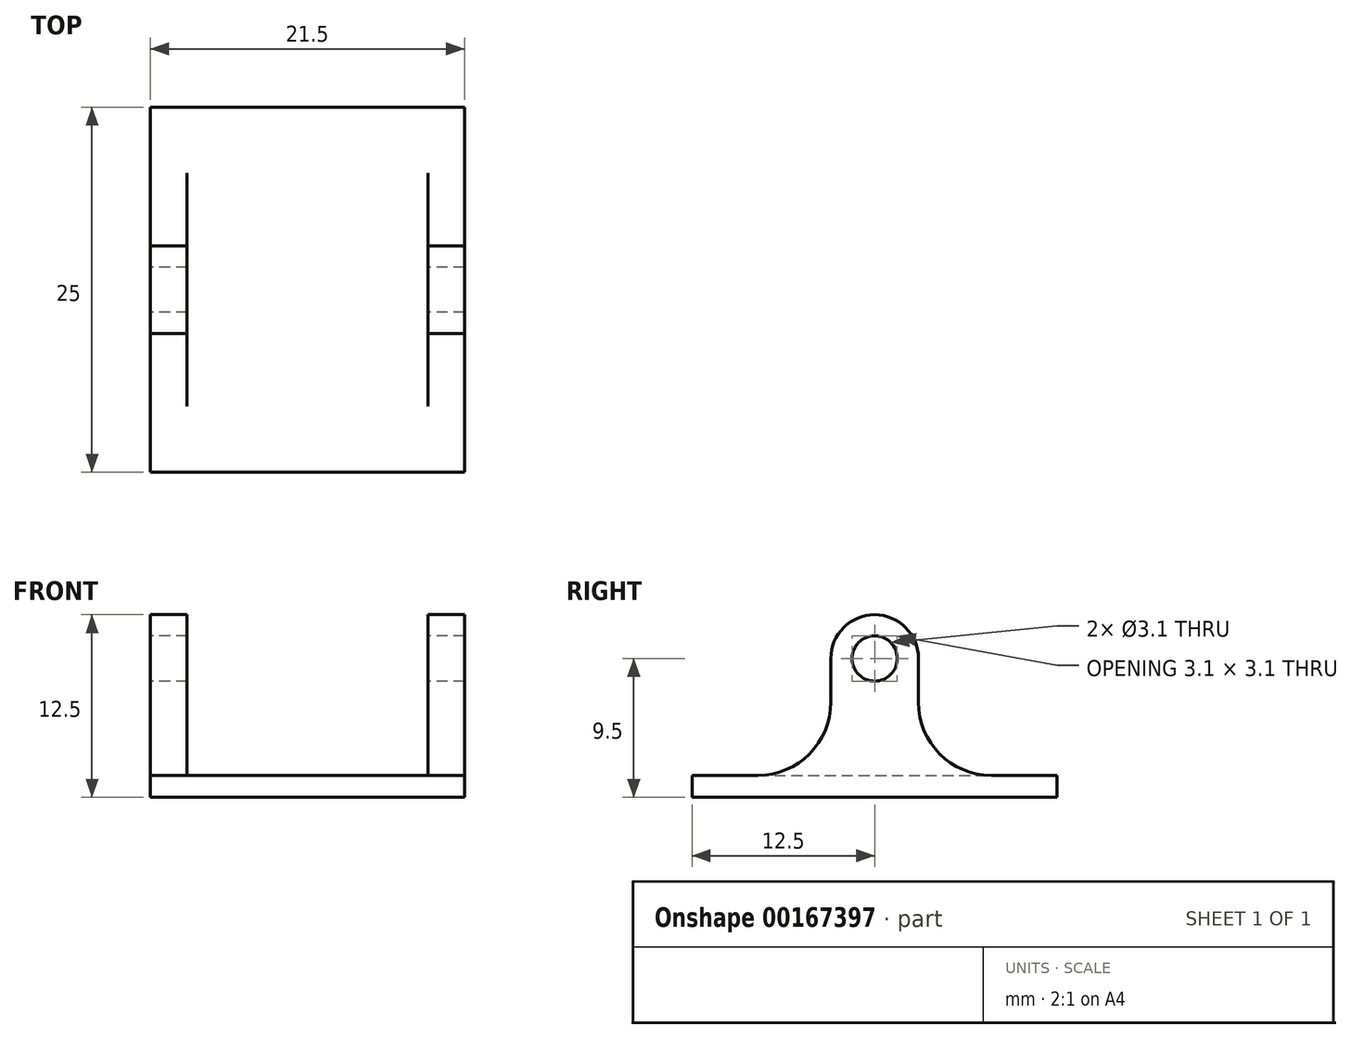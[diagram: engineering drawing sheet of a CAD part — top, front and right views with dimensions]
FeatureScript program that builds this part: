
annotation { "Feature Type Name" : "Feature", "Feature Type Description" : "" }
export const myFeature = defineFeature(function(context is Context, id is Id, definition is map)
    precondition{}
    {
        {
            var Q0;
            Q0=qCreatedBy(makeId("Front.planeOp"),FACE);
            var sketch = newSketch(context, id + "F0", { "sketchPlane" : qUnion([Q0])});
            skLineSegment(sketch, "E0.bottom", {"start": v(5.75, 3) * mm, "end": v(-5.75, 3) * mm, "construction": true});
            skLineSegment(sketch, "E0.top", {"start": v(5.75, -3) * mm, "end": v(-5.75, -3) * mm, "construction": true});
            skLineSegment(sketch, "E0.left", {"start": v(5.75, 3) * mm, "end": v(5.75, -3) * mm, "construction": true});
            skLineSegment(sketch, "E0.right", {"start": v(-5.75, 3) * mm, "end": v(-5.75, -3) * mm, "construction": true});
            skPoint(sketch, "E0.middle", {"position": v(0, 0) * mm});
            skArc(sketch, "E1", {"start": v(-2.75, 3) * mm, "mid": v(-5.75, 0) * mm, "end": v(-2.75, -3) * mm, "construction": true});
            skArc(sketch, "E2.MirrorCS", {"start": v(2.75, 3) * mm, "mid": v(5.75, 0) * mm, "end": v(2.75, -3) * mm, "construction": true});
            skLineSegment(sketch, "E3", {"start": v(-2.75, 3) * mm, "end": v(2.75, 3) * mm, "construction": true});
            skLineSegment(sketch, "E4", {"start": v(-2.75, -3) * mm, "end": v(2.75, -3) * mm, "construction": true});
            skArc(sketch, "E5.0", {"start": v(-2.75, 4.25) * mm, "mid": v(-7, 0) * mm, "end": v(-2.75, -4.25) * mm});
            skLineSegment(sketch, "E5.1", {"start": v(-2.75, 4.25) * mm, "end": v(2.75, 4.25) * mm});
            skArc(sketch, "E5.2", {"start": v(2.75, 4.25) * mm, "mid": v(7, 0) * mm, "end": v(2.75, -4.25) * mm});
            skLineSegment(sketch, "E5.3", {"start": v(-2.75, -4.25) * mm, "end": v(2.75, -4.25) * mm});
            skArc(sketch, "E6.0", {"start": v(-2.75, 3.2) * mm, "mid": v(-5.95, 0) * mm, "end": v(-2.75, -3.2) * mm});
            skLineSegment(sketch, "E6.1", {"start": v(-2.75, 3.2) * mm, "end": v(2.75, 3.2) * mm});
            skArc(sketch, "E6.2", {"start": v(2.75, 3.2) * mm, "mid": v(5.95, 0) * mm, "end": v(2.75, -3.2) * mm});
            skLineSegment(sketch, "E6.3", {"start": v(-2.75, -3.2) * mm, "end": v(2.75, -3.2) * mm});
            skSolve(sketch);
        }
        {
            var Q0;
            Q0=qCreatedBy(makeId("Right.planeOp"),FACE);
            var sketch = newSketch(context, id + "F1", { "sketchPlane" : qUnion([Q0])});
            skCircle(sketch, "E7", {"center": v(0, 0) * mm, "radius": 1.55 * mm});
            skCircle(sketch, "E8", {"center": v(0, 0) * mm, "radius": 3 * mm});
            skSolve(sketch);
        }
        {
            var Q0;
            Q0 = qSketchRegion(id + "F0", true);
            extrude(context, id + "F2", {"entities" : qUnion([Q0]), "endBound" : BoundingType.SYMMETRIC, "depth" : 15 * mm});
        }
        {
            var Q0;
            Q0=makeQuery(id+"F1.imprint","IMPRINT",FACE,{"disambiguationData":[TD([[makeQuery(id+"F1.imprint","IMPRINT",EDGE,{"derivedFrom":sQuery(id+"F1.wireOp",EDGE,"E7")}),-1.0]])]});
            extrude(context, id + "F3", {"entities" : qUnion([Q0]), "operationType" : NewBodyOperationType.ADD, "endBound" : BoundingType.SYMMETRIC, "depth" : (11.5 + 5) * mm});
        }
        {
            var Q0;
            Q0=makeQuery(id+"F1.imprint","IMPRINT",FACE,{"disambiguationData":[TD([[makeQuery(id+"F1.imprint","IMPRINT",EDGE,{"derivedFrom":sQuery(id+"F1.wireOp",EDGE,"E7")}),1.0]])]});
            extrude(context, id + "F4", {"entities" : qUnion([Q0]), "operationType" : NewBodyOperationType.REMOVE, "endBound" : BoundingType.SYMMETRIC, "oppositeDirection" : true, "depth" : 16.5 * mm});
        }
        {
            var Q0;
            Q0=makeQuery(id+"F0.imprint","IMPRINT",FACE,{"disambiguationData":[TD([[makeQuery(id+"F0.imprint","IMPRINT",EDGE,{"derivedFrom":sQuery(id+"F0.wireOp",EDGE,"E6.0")}),1.0]])]});
            extrude(context, id + "F5", {"entities" : qUnion([Q0]), "operationType" : NewBodyOperationType.REMOVE, "endBound" : BoundingType.SYMMETRIC, "oppositeDirection" : true, "depth" : 15 * mm});
        }
        {
            var Q0;
            Q0=qCreatedBy(makeId("Right.planeOp"),FACE);
            var sketch = newSketch(context, id + "F6", { "sketchPlane" : qUnion([Q0])});
            skCircle(sketch, "E9", {"center": v(0, 0) * mm, "radius": 1.55 * mm});
            skArc(sketch, "E10", {"start": v(-3, 0) * mm, "mid": v(0, 3) * mm, "end": v(3, 0) * mm});
            skLineSegment(sketch, "E11.bottom", {"start": v(-12.5, -8) * mm, "end": v(-3, -8) * mm});
            skLineSegment(sketch, "E11.top", {"start": v(-12.5, -9.5) * mm, "end": v(12.5, -9.5) * mm});
            skLineSegment(sketch, "E11.left", {"start": v(-12.5, -8) * mm, "end": v(-12.5, -9.5) * mm});
            skLineSegment(sketch, "E11.right", {"start": v(12.5, -8) * mm, "end": v(12.5, -9.5) * mm});
            skPoint(sketch, "E11.middle", {"position": v(0, -8.75) * mm});
            skLineSegment(sketch, "E12", {"start": v(-3, 0) * mm, "end": v(-3, -8) * mm});
            skLineSegment(sketch, "E13", {"start": v(3, 0) * mm, "end": v(3, -8) * mm});
            skLineSegment(sketch, "E14.trimOffspring", {"start": v(3, -8) * mm, "end": v(12.5, -8) * mm});
            skSolve(sketch);
        }
        {
            var Q0;
            Q0=makeQuery(id+"F6.imprint","IMPRINT",FACE,{"disambiguationData":[TD([[makeQuery(id+"F6.imprint","IMPRINT",EDGE,{"derivedFrom":sQuery(id+"F6.wireOp",EDGE,"E9")}),-1.0]])]});
            extrude(context, id + "F7", {"entities" : qUnion([Q0]), "endBound" : BoundingType.SYMMETRIC, "depth" : (16.5 + 5) * mm});
        }
        {
            var Q0;
            Q0=makeQuery(id+"F7.opExtrude","SWEPT_EDGE",EDGE,{"disambiguationData":[OSD([sQuery(id+"F6.wireOp",EDGE,"E13"),sQuery(id+"F6.wireOp",EDGE,"E14.trimOffspring")])]});
            var Q1;
            Q1=makeQuery(id+"F7.opExtrude","SWEPT_EDGE",EDGE,{"disambiguationData":[OSD([sQuery(id+"F6.wireOp",EDGE,"E11.bottom"),sQuery(id+"F6.wireOp",EDGE,"E12")])]});
            fillet(context, id + "F8", {"entities" : qUnion([Q0, Q1]), "radius" : 5 * mm, "allowEdgeOverflow" : false});
        }
        {
            var Q0;
            Q0=qCreatedBy(makeId("Front.planeOp"),FACE);
            var sketch = newSketch(context, id + "F9", { "sketchPlane" : qUnion([Q0])});
            skLineSegment(sketch, "E15.0.0", {"start": v(-10.75, -8) * mm, "end": v(-10.75, -9.5) * mm, "construction": true});
            skLineSegment(sketch, "E15.0.1", {"start": v(-10.75, -9.5) * mm, "end": v(10.75, -9.5) * mm, "construction": true});
            skLineSegment(sketch, "E15.0.2", {"start": v(10.75, -9.5) * mm, "end": v(10.75, -8) * mm, "construction": true});
            skLineSegment(sketch, "E15.0.3", {"start": v(10.75, -8) * mm, "end": v(-10.75, -8) * mm, "construction": true});
            skLineSegment(sketch, "E16.bottom", {"start": v(-8.25, -8) * mm, "end": v(8.25, -8) * mm});
            skLineSegment(sketch, "E16.top", {"start": v(-8.25, 8) * mm, "end": v(8.25, 8) * mm});
            skLineSegment(sketch, "E16.left", {"start": v(-8.25, -8) * mm, "end": v(-8.25, 8) * mm});
            skLineSegment(sketch, "E16.right", {"start": v(8.25, -8) * mm, "end": v(8.25, 8) * mm});
            skPoint(sketch, "E16.middle", {"position": v(0, 0) * mm});
            skSolve(sketch);
        }
        {
            var Q0;
            Q0 = qSketchRegion(id + "F9", true);
            var Q1;
            Q1 = qConstructionFilter(qBodyType(qCreatedBy(id + "F9" ,EDGE), BodyType.WIRE), ConstructionObject.NO);
            var Q2;
            Q2=makeQuery(id+"F7.opExtrude","SWEPT_FACE",FACE,{"disambiguationData":[OSD([sQuery(id+"F6.wireOp",EDGE,"E11.left")])]});
            extrude(context, id + "F10", {"entities" : qUnion([Q0]), "operationType" : NewBodyOperationType.REMOVE, "surfaceEntities" : qUnion([Q1]), "endBound" : BoundingType.THROUGH_ALL, "endBoundEntityFace" : qUnion([Q2]), "depth" : 25 * mm, "hasSecondDirection" : true, "secondDirectionBound" : SecondDirectionBoundingType.THROUGH_ALL, "secondDirectionOppositeDirection" : true, "secondDirectionDepth" : 25 * mm});
        }
    });
